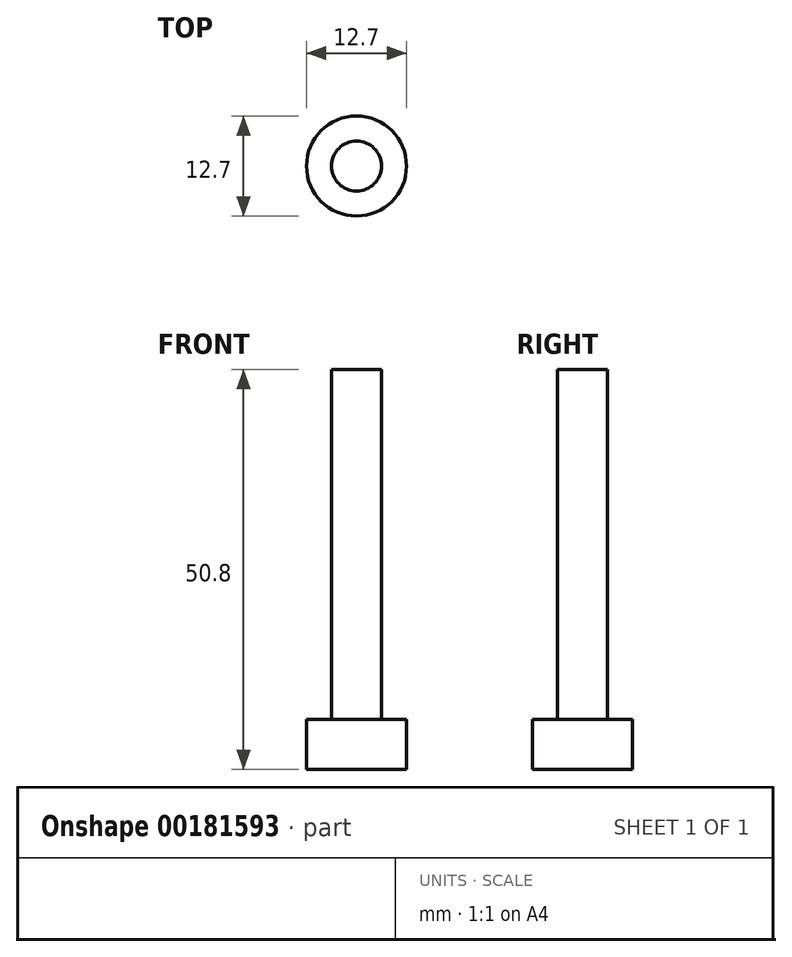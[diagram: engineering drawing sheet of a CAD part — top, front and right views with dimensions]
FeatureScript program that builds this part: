
annotation { "Feature Type Name" : "Feature", "Feature Type Description" : "" }
export const myFeature = defineFeature(function(context is Context, id is Id, definition is map)
    precondition{}
    {
        {
            var Q0;
            Q0=qCreatedBy(makeId("Front.planeOp"),FACE);
            var sketch = newSketch(context, id + "F0", { "sketchPlane" : qUnion([Q0])});
            skLineSegment(sketch, "E0", {"start": v(0, 0) * mm, "end": v(6.35, 0) * mm});
            skLineSegment(sketch, "E1", {"start": v(6.35, 0) * mm, "end": v(6.35, 6.35) * mm});
            skLineSegment(sketch, "E2", {"start": v(6.35, 6.35) * mm, "end": v(3.18, 6.35) * mm});
            skLineSegment(sketch, "E3", {"start": v(3.18, 6.35) * mm, "end": v(3.18, 50.8) * mm});
            skLineSegment(sketch, "E4", {"start": v(3.18, 50.8) * mm, "end": v(0, 50.8) * mm});
            skLineSegment(sketch, "E5", {"start": v(0, 50.8) * mm, "end": v(0, 0) * mm});
            skSolve(sketch);
        }
        {
            var Q0;
            Q0 = qSketchRegion(id + "F0", true);
            var Q1;
            Q1=sQuery(id+"F0.wireOp",EDGE,"E5");
            revolve(context, id + "F1", {"entities" : qUnion([Q0]), "axis" : qUnion([Q1]), "revolveType" : RevolveType.FULL});
        }
    });
